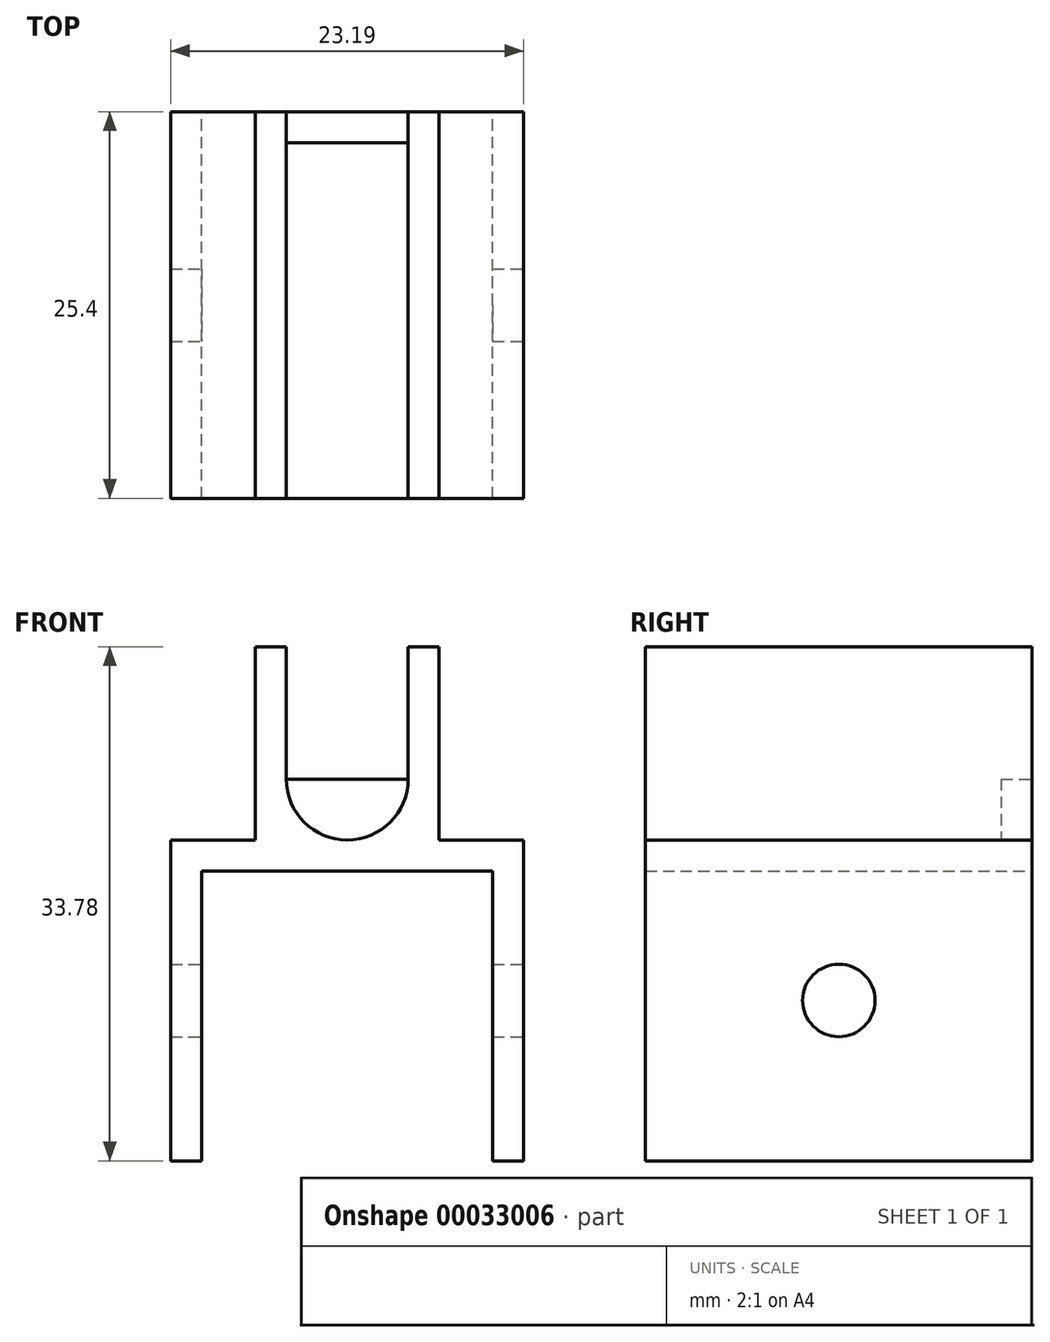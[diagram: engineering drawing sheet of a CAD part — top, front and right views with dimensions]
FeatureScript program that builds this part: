
annotation { "Feature Type Name" : "Feature", "Feature Type Description" : "" }
export const myFeature = defineFeature(function(context is Context, id is Id, definition is map)
    precondition{}
    {
        {
            var Q0;
            Q0=qCreatedBy(makeId("Front.planeOp"),FACE);
            var sketch = newSketch(context, id + "F0", { "sketchPlane" : qUnion([Q0])});
            skLineSegment(sketch, "E0.bottom", {"start": v(0, 0) * mm, "end": v(23.2, 0) * mm});
            skLineSegment(sketch, "E0.top", {"start": v(0, 21.08) * mm, "end": v(23.2, 21.08) * mm});
            skLineSegment(sketch, "E0.left", {"start": v(0, 0) * mm, "end": v(0, 21.08) * mm});
            skLineSegment(sketch, "E0.right", {"start": v(23.2, 0) * mm, "end": v(23.2, 21.08) * mm});
            skLineSegment(sketch, "E1.bottom", {"start": v(2.03, 0) * mm, "end": v(21.16, 0) * mm});
            skLineSegment(sketch, "E1.top", {"start": v(2.03, 19.05) * mm, "end": v(21.16, 19.05) * mm});
            skLineSegment(sketch, "E1.left", {"start": v(2.03, 0) * mm, "end": v(2.03, 19.05) * mm});
            skLineSegment(sketch, "E1.right", {"start": v(21.16, 0) * mm, "end": v(21.16, 19.05) * mm});
            skLineSegment(sketch, "E2.bottom", {"start": v(5.56, 21.08) * mm, "end": v(17.63, 21.08) * mm});
            skLineSegment(sketch, "E2.top", {"start": v(5.56, 33.78) * mm, "end": v(17.63, 33.78) * mm});
            skLineSegment(sketch, "E2.left", {"start": v(5.56, 21.08) * mm, "end": v(5.56, 33.78) * mm});
            skLineSegment(sketch, "E2.right", {"start": v(17.63, 21.08) * mm, "end": v(17.63, 33.78) * mm});
            skLineSegment(sketch, "E3.bottom", {"start": v(7.6, 33.78) * mm, "end": v(15.6, 33.78) * mm});
            skLineSegment(sketch, "E3.top", {"start": v(7.6, 25.08) * mm, "end": v(15.6, 25.08) * mm});
            skLineSegment(sketch, "E3.left", {"start": v(7.6, 33.78) * mm, "end": v(7.6, 25.08) * mm});
            skLineSegment(sketch, "E3.right", {"start": v(15.6, 33.78) * mm, "end": v(15.6, 25.08) * mm});
            skArc(sketch, "E4", {"start": v(7.6, 25.08) * mm, "mid": v(11.6, 21.08) * mm, "end": v(15.6, 25.08) * mm});
            skLineSegment(sketch, "E5", {"start": v(17.63, 21.08) * mm, "end": v(23.2, 21.08) * mm});
            skLineSegment(sketch, "E6", {"start": v(5.56, 21.08) * mm, "end": v(0, 21.08) * mm});
            skSolve(sketch);
        }
        {
            var Q0;
            {var subQ1=sQuery(id+"F0.wireOp",EDGE,"E0.left");Q0=makeQuery(id+"F0.imprint","IMPRINT",FACE,{"disambiguationData":[TD([[makeQuery(id+"F0.imprint","IMPRINT",EDGE,{"derivedFrom":subQ1}),-1.0]])]});}
            var Q1;
            {var subQ1=sQuery(id+"F0.wireOp",EDGE,"E2.right");Q1=makeQuery(id+"F0.imprint","IMPRINT",FACE,{"disambiguationData":[TD([[makeQuery(id+"F0.imprint","IMPRINT",EDGE,{"derivedFrom":subQ1}),1.0]])]});}
            var Q2;
            {var subQ1=sQuery(id+"F0.wireOp",EDGE,"E2.left");Q2=makeQuery(id+"F0.imprint","IMPRINT",FACE,{"disambiguationData":[TD([[makeQuery(id+"F0.imprint","IMPRINT",EDGE,{"derivedFrom":subQ1}),-1.0]])]});}
            extrude(context, id + "F1", {"entities" : qUnion([Q0, Q1, Q2]), "depth" : 25.4 * mm});
        }
        {
            var Q0;
            {var subQ0=sQuery(id+"F0.wireOp",EDGE,"E3.top");Q0=makeQuery(id+"F0.imprint","IMPRINT",FACE,{"disambiguationData":[TD([[makeQuery(id+"F0.imprint","IMPRINT",EDGE,{"derivedFrom":subQ0}),-1.0]])]});}
            var Q1;
            Q1=makeQuery(id+"F0.imprint","IMPRINT",FACE,{"disambiguationData":[TD([[makeQuery(id+"F0.imprint","IMPRINT",EDGE,{"derivedFrom":sQuery(id+"F0.wireOp",EDGE,"E3.bottom")}),-1.0]])]});
            extrude(context, id + "F2", {"entities" : qUnion([Q0, Q1]), "operationType" : NewBodyOperationType.ADD, "depth" : 2.03 * mm});
        }
        {
            var Q0;
            Q0=makeQuery(id+"F1.opExtrude","SWEPT_FACE",FACE,{"disambiguationData":[OSD([sQuery(id+"F0.wireOp",EDGE,"E0.right")])]});
            var sketch = newSketch(context, id + "F3", { "sketchPlane" : qUnion([Q0])});
            skLineSegment(sketch, "E7", {"start": v(-12.7, 21.08) * mm, "end": v(-12.7, 0) * mm, "construction": true});
            skLineSegment(sketch, "E8", {"start": v(-25.4, 10.54) * mm, "end": v(0, 10.54) * mm, "construction": true});
            skPoint(sketch, "E9", {"position": v(-12.7, 10.54) * mm});
            skSolve(sketch);
        }
        {
            var Q0;
            Q0=sQuery(id+"F3.wireOp",VERTEX,"E9");
            var Q1;
            Q1=makeQuery(id+"F1.opExtrude","SWEPT_BODY",BODY,{"disambiguationData":[OSD([sQuery(id+"F0.wireOp",EDGE,"E0.bottom"),sQuery(id+"F0.wireOp",EDGE,"E0.left"),sQuery(id+"F0.wireOp",EDGE,"E0.right"),sQuery(id+"F0.wireOp",EDGE,"E1.top"),sQuery(id+"F0.wireOp",EDGE,"E1.left"),sQuery(id+"F0.wireOp",EDGE,"E1.right"),sQuery(id+"F0.wireOp",EDGE,"E2.top"),sQuery(id+"F0.wireOp",EDGE,"E2.left"),sQuery(id+"F0.wireOp",EDGE,"E2.right"),sQuery(id+"F0.wireOp",EDGE,"E3.left"),sQuery(id+"F0.wireOp",EDGE,"E3.right"),sQuery(id+"F0.wireOp",EDGE,"E4"),sQuery(id+"F0.wireOp",EDGE,"E5"),sQuery(id+"F0.wireOp",EDGE,"E6")])]});
            hole(context, id + "F4", {"style" : HoleStyle.SIMPLE, "endStyle" : HoleEndStyle.THROUGH, "holeDiameter" : 4.76 * mm, "locations" : qUnion([Q0]), "scope" : qUnion([Q1]), "isTappedThrough" : true});
        }
    });
